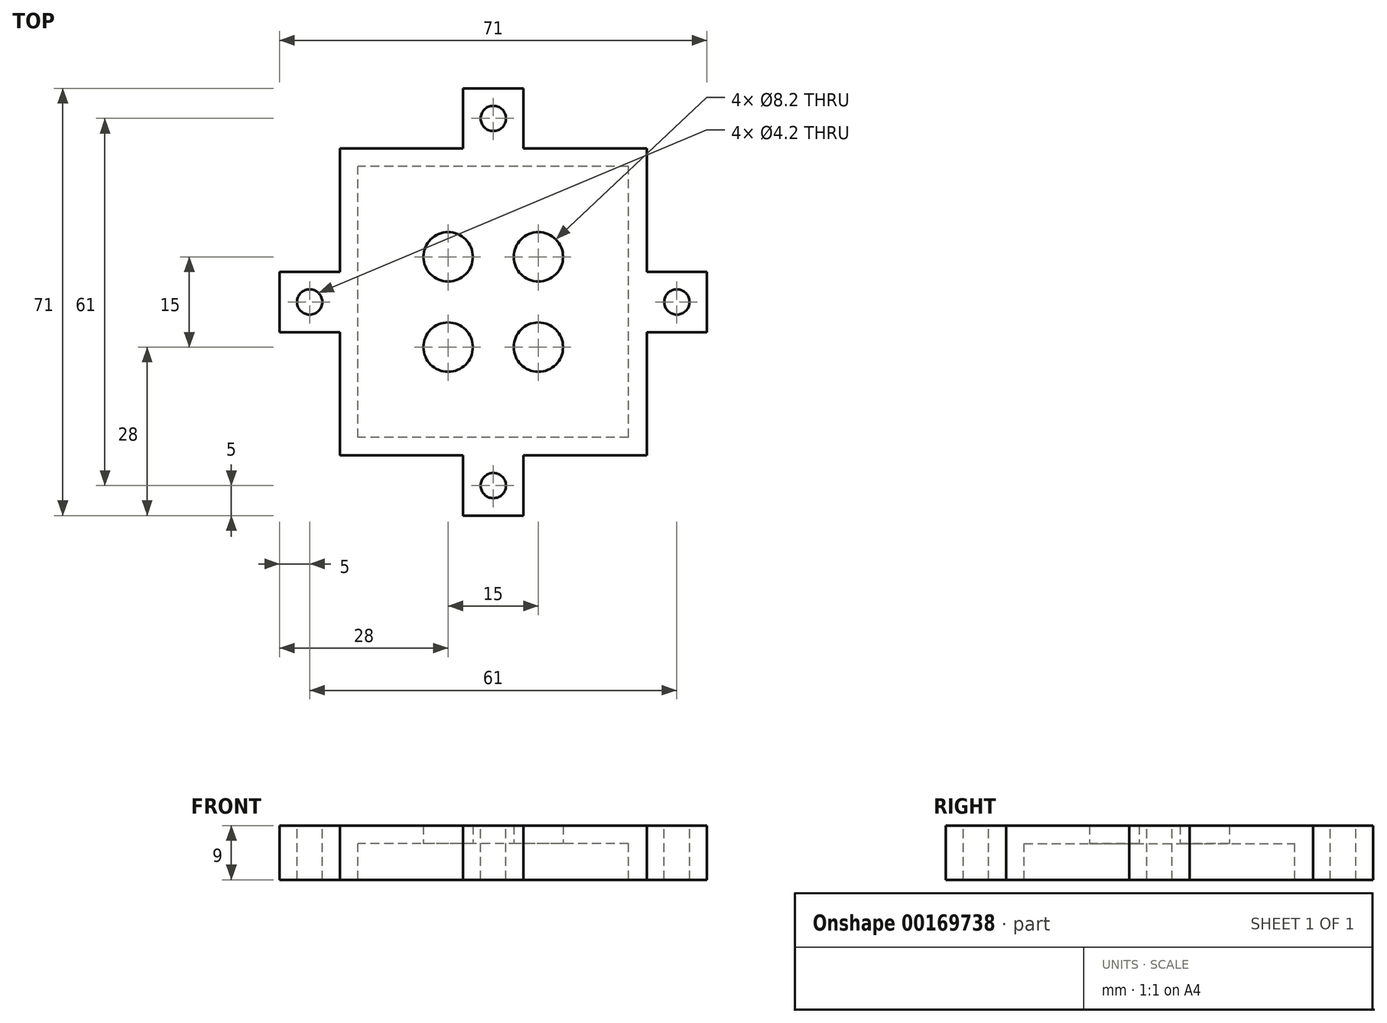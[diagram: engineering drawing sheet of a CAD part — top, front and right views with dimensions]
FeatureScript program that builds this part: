
annotation { "Feature Type Name" : "Feature", "Feature Type Description" : "" }
export const myFeature = defineFeature(function(context is Context, id is Id, definition is map)
    precondition{}
    {
        {
            var Q0;
            Q0=qCreatedBy(makeId("Top.planeOp"),FACE);
            var sketch = newSketch(context, id + "F0", { "sketchPlane" : qUnion([Q0])});
            skLineSegment(sketch, "E0.bottom", {"start": v(22.5, -22.5) * mm, "end": v(-22.5, -22.5) * mm});
            skLineSegment(sketch, "E0.top", {"start": v(22.5, 22.5) * mm, "end": v(-22.5, 22.5) * mm});
            skLineSegment(sketch, "E0.left", {"start": v(22.5, -22.5) * mm, "end": v(22.5, 22.5) * mm});
            skLineSegment(sketch, "E0.right", {"start": v(-22.5, -22.5) * mm, "end": v(-22.5, 22.5) * mm});
            skPoint(sketch, "E0.middle", {"position": v(0, 0) * mm});
            skCircle(sketch, "E1", {"center": v(-7.5, 7.5) * mm, "radius": 4.1 * mm});
            skCircle(sketch, "E2", {"center": v(7.5, 7.5) * mm, "radius": 4.1 * mm});
            skCircle(sketch, "E3", {"center": v(-7.5, -7.5) * mm, "radius": 4.1 * mm});
            skCircle(sketch, "E4", {"center": v(7.5, -7.5) * mm, "radius": 4.1 * mm});
            skSolve(sketch);
        }
        {
            var Q0;
            Q0=makeQuery(id+"F0.imprint","IMPRINT",FACE,{"disambiguationData":[TD([[makeQuery(id+"F0.imprint","IMPRINT",EDGE,{"derivedFrom":sQuery(id+"F0.wireOp",EDGE,"E0.bottom")}),-1.0]])]});
            extrude(context, id + "F1", {"entities" : qUnion([Q0]), "depth" : 3 * mm});
        }
        {
            var Q0;
            Q0=makeQuery(id+"F1.opExtrude","CAP_FACE",FACE,{"disambiguationData":[OSD([sQuery(id+"F0.wireOp",EDGE,"E0.bottom"),sQuery(id+"F0.wireOp",EDGE,"E0.top"),sQuery(id+"F0.wireOp",EDGE,"E0.left"),sQuery(id+"F0.wireOp",EDGE,"E0.right"),sQuery(id+"F0.wireOp",EDGE,"E1"),sQuery(id+"F0.wireOp",EDGE,"E2"),sQuery(id+"F0.wireOp",EDGE,"E3"),sQuery(id+"F0.wireOp",EDGE,"E4")])],"isStart":false});
            var sketch = newSketch(context, id + "F2", { "sketchPlane" : qUnion([Q0])});
            skLineSegment(sketch, "E5.bottom", {"start": v(-25.5, 25.5) * mm, "end": v(25.5, 25.5) * mm});
            skLineSegment(sketch, "E5.top", {"start": v(-25.5, -25.5) * mm, "end": v(25.5, -25.5) * mm});
            skLineSegment(sketch, "E5.left", {"start": v(-25.5, 25.5) * mm, "end": v(-25.5, -25.5) * mm});
            skLineSegment(sketch, "E5.right", {"start": v(25.5, 25.5) * mm, "end": v(25.5, -25.5) * mm});
            skPoint(sketch, "E5.middle", {"position": v(0, 0) * mm});
            skLineSegment(sketch, "E6.bottom", {"start": v(22.5, 22.5) * mm, "end": v(-22.5, 22.5) * mm});
            skLineSegment(sketch, "E6.top", {"start": v(22.5, -22.5) * mm, "end": v(-22.5, -22.5) * mm});
            skLineSegment(sketch, "E6.left", {"start": v(22.5, 22.5) * mm, "end": v(22.5, -22.5) * mm});
            skLineSegment(sketch, "E6.right", {"start": v(-22.5, 22.5) * mm, "end": v(-22.5, -22.5) * mm});
            skSolve(sketch);
        }
        {
            var Q0;
            Q0=makeQuery(id+"F2.imprint","IMPRINT",FACE,{"disambiguationData":[TD([[makeQuery(id+"F2.imprint","IMPRINT",EDGE,{"derivedFrom":sQuery(id+"F2.wireOp",EDGE,"E5.bottom")}),-1.0]])]});
            extrude(context, id + "F3", {"entities" : qUnion([Q0]), "operationType" : NewBodyOperationType.ADD, "oppositeDirection" : true, "depth" : 9 * mm});
        }
        {
            var Q0;
            Q0=makeQuery(id+"F3.boolean.opBoolean","MERGE",FACE,{"derivedFrom":[makeQuery(id+"F1.opExtrude","CAP_FACE",FACE,{"disambiguationData":[OSD([sQuery(id+"F0.wireOp",EDGE,"E0.bottom"),sQuery(id+"F0.wireOp",EDGE,"E0.top"),sQuery(id+"F0.wireOp",EDGE,"E0.left"),sQuery(id+"F0.wireOp",EDGE,"E0.right"),sQuery(id+"F0.wireOp",EDGE,"E1"),sQuery(id+"F0.wireOp",EDGE,"E2"),sQuery(id+"F0.wireOp",EDGE,"E3"),sQuery(id+"F0.wireOp",EDGE,"E4")])],"isStart":false}),makeQuery(id+"F3.opExtrude","CAP_FACE",FACE,{"disambiguationData":[OSD([sQuery(id+"F2.wireOp",EDGE,"E5.bottom"),sQuery(id+"F2.wireOp",EDGE,"E5.top"),sQuery(id+"F2.wireOp",EDGE,"E5.left"),sQuery(id+"F2.wireOp",EDGE,"E5.right"),sQuery(id+"F2.wireOp",EDGE,"E6.bottom"),sQuery(id+"F2.wireOp",EDGE,"E6.top"),sQuery(id+"F2.wireOp",EDGE,"E6.left"),sQuery(id+"F2.wireOp",EDGE,"E6.right")])],"isStart":true})]});
            var sketch = newSketch(context, id + "F4", { "sketchPlane" : qUnion([Q0])});
            skLineSegment(sketch, "E7.bottom", {"start": v(5, -25.5) * mm, "end": v(-5, -25.5) * mm});
            skLineSegment(sketch, "E7.top", {"start": v(5, -35.5) * mm, "end": v(-5, -35.5) * mm});
            skLineSegment(sketch, "E7.left", {"start": v(5, -25.5) * mm, "end": v(5, -35.5) * mm});
            skLineSegment(sketch, "E7.right", {"start": v(-5, -25.5) * mm, "end": v(-5, -35.5) * mm});
            skLineSegment(sketch, "E8.bottom", {"start": v(25.5, -5) * mm, "end": v(35.5, -5) * mm});
            skLineSegment(sketch, "E8.top", {"start": v(25.5, 5) * mm, "end": v(35.5, 5) * mm});
            skLineSegment(sketch, "E8.left", {"start": v(25.5, -5) * mm, "end": v(25.5, 5) * mm});
            skLineSegment(sketch, "E8.right", {"start": v(35.5, -5) * mm, "end": v(35.5, 5) * mm});
            skLineSegment(sketch, "E9.bottom", {"start": v(5, 25.5) * mm, "end": v(-5, 25.5) * mm});
            skLineSegment(sketch, "E9.top", {"start": v(5, 35.5) * mm, "end": v(-5, 35.5) * mm});
            skLineSegment(sketch, "E9.left", {"start": v(5, 25.5) * mm, "end": v(5, 35.5) * mm});
            skLineSegment(sketch, "E9.right", {"start": v(-5, 25.5) * mm, "end": v(-5, 35.5) * mm});
            skLineSegment(sketch, "E10.bottom", {"start": v(-25.5, 5) * mm, "end": v(-35.5, 5) * mm});
            skLineSegment(sketch, "E10.top", {"start": v(-25.5, -5) * mm, "end": v(-35.5, -5) * mm});
            skLineSegment(sketch, "E10.left", {"start": v(-25.5, 5) * mm, "end": v(-25.5, -5) * mm});
            skLineSegment(sketch, "E10.right", {"start": v(-35.5, 5) * mm, "end": v(-35.5, -5) * mm});
            skPoint(sketch, "E11", {"position": v(0, -25.5) * mm});
            skPoint(sketch, "E12", {"position": v(25.5, 0) * mm});
            skPoint(sketch, "E13", {"position": v(0, 25.5) * mm});
            skPoint(sketch, "E14", {"position": v(-25.5, 0) * mm});
            skCircle(sketch, "E15", {"center": v(30.5, 0) * mm, "radius": 2.1 * mm});
            skPoint(sketch, "E15.centerSnap0", {"position": v(35.5, 0) * mm});
            skPoint(sketch, "E15.centerSnap1", {"position": v(30.5, -5) * mm});
            skCircle(sketch, "E16", {"center": v(0, -30.5) * mm, "radius": 2.1 * mm});
            skPoint(sketch, "E16.centerSnap0", {"position": v(5, -30.5) * mm});
            skPoint(sketch, "E16.centerSnap1", {"position": v(0, -35.5) * mm});
            skCircle(sketch, "E17", {"center": v(-30.5, 0) * mm, "radius": 2.1 * mm});
            skPoint(sketch, "E17.centerSnap0", {"position": v(-30.5, 5) * mm});
            skCircle(sketch, "E18", {"center": v(0, 30.5) * mm, "radius": 2.1 * mm});
            skPoint(sketch, "E18.centerSnap0", {"position": v(-5, 30.5) * mm});
            skSolve(sketch);
        }
        {
            var Q0;
            Q0=makeQuery(id+"F4.imprint","IMPRINT",FACE,{"disambiguationData":[TD([[makeQuery(id+"F4.imprint","IMPRINT",EDGE,{"derivedFrom":sQuery(id+"F4.wireOp",EDGE,"E9.bottom")}),1.0]])]});
            var Q1;
            Q1=makeQuery(id+"F4.imprint","IMPRINT",FACE,{"disambiguationData":[TD([[makeQuery(id+"F4.imprint","IMPRINT",EDGE,{"derivedFrom":sQuery(id+"F4.wireOp",EDGE,"E10.bottom")}),1.0]])]});
            var Q2;
            Q2=makeQuery(id+"F4.imprint","IMPRINT",FACE,{"disambiguationData":[TD([[makeQuery(id+"F4.imprint","IMPRINT",EDGE,{"derivedFrom":sQuery(id+"F4.wireOp",EDGE,"E7.bottom")}),-1.0]])]});
            var Q3;
            Q3=makeQuery(id+"F4.imprint","IMPRINT",FACE,{"disambiguationData":[TD([[makeQuery(id+"F4.imprint","IMPRINT",EDGE,{"derivedFrom":sQuery(id+"F4.wireOp",EDGE,"E8.bottom")}),1.0]])]});
            extrude(context, id + "F5", {"entities" : qUnion([Q0, Q1, Q2, Q3]), "operationType" : NewBodyOperationType.ADD, "oppositeDirection" : true, "depth" : 9 * mm});
        }
    });
